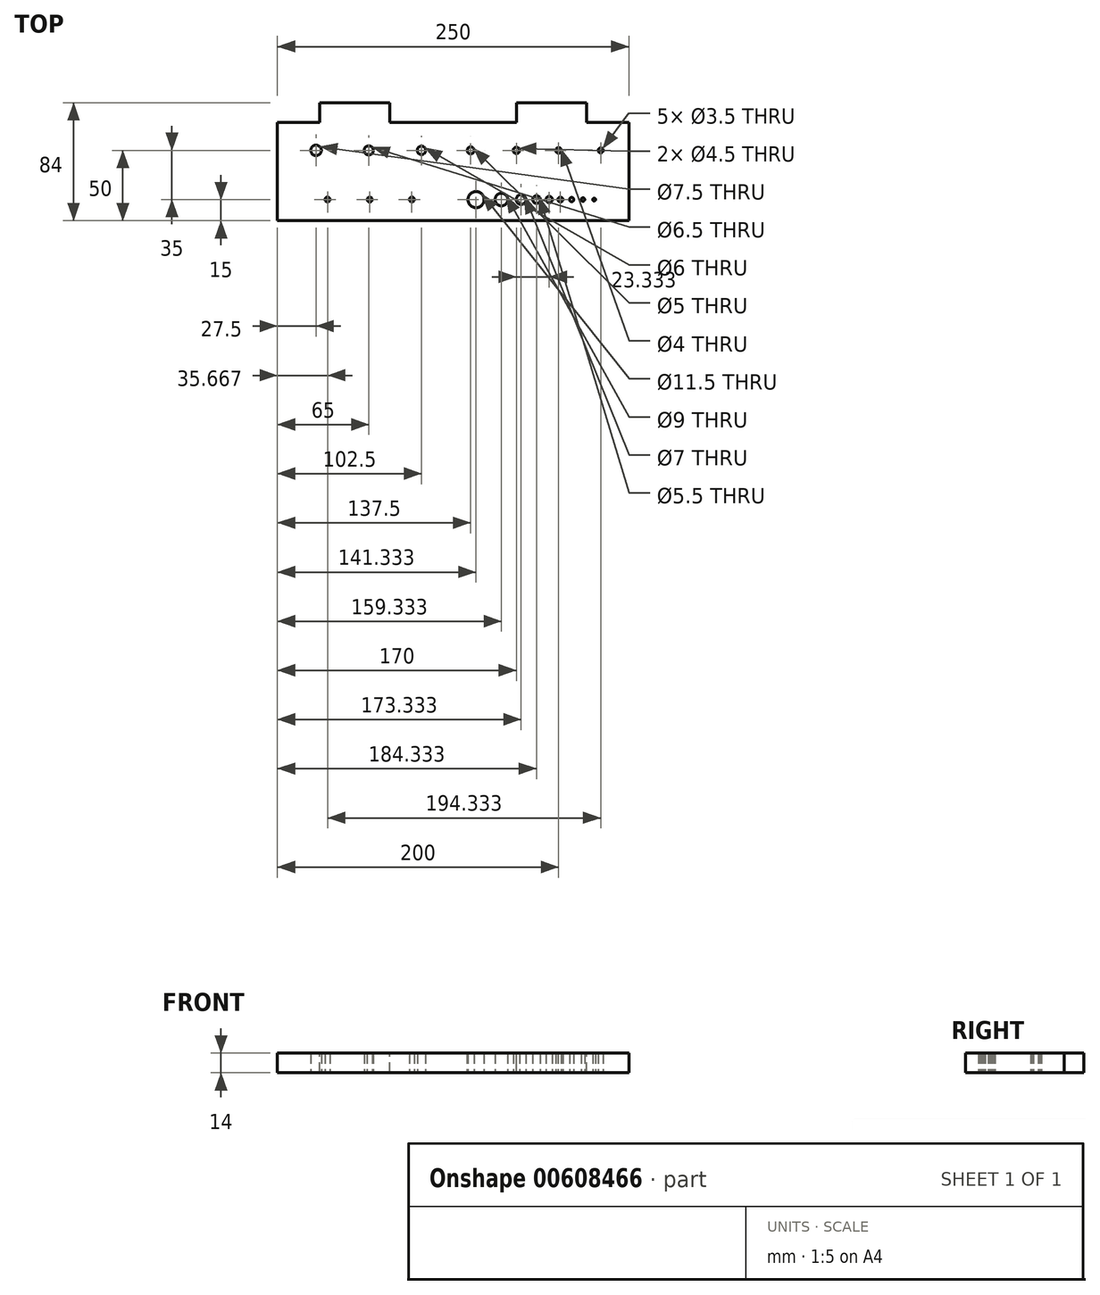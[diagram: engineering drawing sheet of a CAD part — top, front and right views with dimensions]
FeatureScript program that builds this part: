
annotation { "Feature Type Name" : "Feature", "Feature Type Description" : "" }
export const myFeature = defineFeature(function(context is Context, id is Id, definition is map)
    precondition{}
    {
        {
            var Q0;
            Q0=qCreatedBy(makeId("Top.planeOp"),FACE);
            var sketch = newSketch(context, id + "F0", { "sketchPlane" : qUnion([Q0])});
            skLineSegment(sketch, "E0.bottom", {"start": v(-125, 0) * mm, "end": v(125, 0) * mm});
            skLineSegment(sketch, "E0.top", {"start": v(-125, -70) * mm, "end": v(125, -70) * mm});
            skLineSegment(sketch, "E0.left", {"start": v(-125, 0) * mm, "end": v(-125, -70) * mm});
            skLineSegment(sketch, "E0.right", {"start": v(125, 0) * mm, "end": v(125, -70) * mm});
            skPoint(sketch, "E1", {"position": v(0, 0) * mm});
            skPoint(sketch, "E2", {"position": v(125, -35) * mm});
            skCircle(sketch, "E3", {"center": v(-97.5, -20) * mm, "radius": 3.75 * mm});
            skCircle(sketch, "E4", {"center": v(-60, -20) * mm, "radius": 3.25 * mm});
            skCircle(sketch, "E5", {"center": v(-22.5, -20) * mm, "radius": 3 * mm});
            skCircle(sketch, "E6", {"center": v(12.5, -20) * mm, "radius": 2.5 * mm});
            skCircle(sketch, "E7", {"center": v(45, -20) * mm, "radius": 2.25 * mm});
            skCircle(sketch, "E8", {"center": v(75, -20) * mm, "radius": 2 * mm});
            skCircle(sketch, "E9", {"center": v(105, -20) * mm, "radius": 1.75 * mm});
            skLineSegment(sketch, "E10", {"start": v(-115, -20) * mm, "end": v(-80, -20) * mm, "construction": true});
            skLineSegment(sketch, "E11", {"start": v(-80, -20) * mm, "end": v(-40, -20) * mm, "construction": true});
            skLineSegment(sketch, "E12", {"start": v(-40, -20) * mm, "end": v(-5, -20) * mm, "construction": true});
            skLineSegment(sketch, "E13", {"start": v(-5, -20) * mm, "end": v(30, -20) * mm, "construction": true});
            skLineSegment(sketch, "E14", {"start": v(30, -20) * mm, "end": v(60, -20) * mm, "construction": true});
            skLineSegment(sketch, "E15", {"start": v(60, -20) * mm, "end": v(90, -20) * mm, "construction": true});
            skLineSegment(sketch, "E16", {"start": v(90, -20) * mm, "end": v(120, -20) * mm, "construction": true});
            skPoint(sketch, "E17", {"position": v(-120, -20) * mm});
            skLineSegment(sketch, "E18", {"start": v(-120, -20) * mm, "end": v(-115, -20) * mm, "construction": true});
            skLineSegment(sketch, "E19", {"start": v(120, -20) * mm, "end": v(125, -20) * mm, "construction": true});
            skLineSegment(sketch, "E20", {"start": v(-120, -20) * mm, "end": v(-125, -20) * mm, "construction": true});
            skLineSegment(sketch, "E21", {"start": v(-125, -55) * mm, "end": v(-104.33, -55) * mm, "construction": true});
            skLineSegment(sketch, "E22", {"start": v(-104.33, -55) * mm, "end": v(-74.33, -55) * mm, "construction": true});
            skLineSegment(sketch, "E23", {"start": v(-74.33, -55) * mm, "end": v(-44.33, -55) * mm, "construction": true});
            skLineSegment(sketch, "E24", {"start": v(-44.33, -55) * mm, "end": v(-14.33, -55) * mm, "construction": true});
            skLineSegment(sketch, "E25", {"start": v(-14.33, -55) * mm, "end": v(6.33, -55) * mm, "construction": true});
            skLineSegment(sketch, "E26", {"start": v(6.33, -55) * mm, "end": v(26.33, -55) * mm, "construction": true});
            skLineSegment(sketch, "E27", {"start": v(26.33, -55) * mm, "end": v(42.33, -55) * mm, "construction": true});
            skLineSegment(sketch, "E28", {"start": v(42.33, -55) * mm, "end": v(54.33, -55) * mm, "construction": true});
            skLineSegment(sketch, "E29", {"start": v(54.33, -55) * mm, "end": v(64.33, -55) * mm, "construction": true});
            skLineSegment(sketch, "E30", {"start": v(64.33, -55) * mm, "end": v(72.33, -55) * mm, "construction": true});
            skLineSegment(sketch, "E31", {"start": v(72.33, -55) * mm, "end": v(80.33, -55) * mm, "construction": true});
            skLineSegment(sketch, "E32", {"start": v(80.33, -55) * mm, "end": v(88.33, -55) * mm, "construction": true});
            skLineSegment(sketch, "E33", {"start": v(88.33, -55) * mm, "end": v(96.33, -55) * mm, "construction": true});
            skLineSegment(sketch, "E34", {"start": v(96.33, -55) * mm, "end": v(104.33, -55) * mm, "construction": true});
            skLineSegment(sketch, "E35", {"start": v(104.33, -55) * mm, "end": v(125, -55) * mm, "construction": true});
            skCircle(sketch, "E36", {"center": v(-89.33, -55) * mm, "radius": 1.75 * mm});
            skCircle(sketch, "E37", {"center": v(-59.33, -55) * mm, "radius": 1.75 * mm});
            skCircle(sketch, "E38", {"center": v(-29.33, -55) * mm, "radius": 1.75 * mm});
            skCircle(sketch, "E39", {"center": v(16.33, -55) * mm, "radius": 5.75 * mm});
            skCircle(sketch, "E40", {"center": v(34.33, -55) * mm, "radius": 4.5 * mm});
            skCircle(sketch, "E41", {"center": v(48.33, -55) * mm, "radius": 3.5 * mm});
            skCircle(sketch, "E42", {"center": v(59.33, -55) * mm, "radius": 2.75 * mm});
            skCircle(sketch, "E43", {"center": v(68.33, -55) * mm, "radius": 2.25 * mm});
            skCircle(sketch, "E44", {"center": v(76.33, -55) * mm, "radius": 1.75 * mm});
            skCircle(sketch, "E45", {"center": v(84.33, -55) * mm, "radius": 1.5 * mm});
            skCircle(sketch, "E46", {"center": v(92.33, -55) * mm, "radius": 1.25 * mm});
            skCircle(sketch, "E47", {"center": v(100.33, -55) * mm, "radius": 1 * mm});
            skSolve(sketch);
        }
        {
            var Q0;
            Q0=makeQuery(id+"F0.imprint","IMPRINT",FACE,{"disambiguationData":[TD([[makeQuery(id+"F0.imprint","IMPRINT",EDGE,{"derivedFrom":sQuery(id+"F0.wireOp",EDGE,"E0.bottom")}),-1.0]])]});
            extrude(context, id + "F1", {"entities" : qUnion([Q0]), "depth" : 14 * mm, "offsetDistance" : 25 * mm});
        }
        {
            var Q0;
            Q0=makeQuery(id+"F1.opExtrude","SWEPT_FACE",FACE,{"disambiguationData":[OSD([sQuery(id+"F0.wireOp",EDGE,"E0.bottom")])]});
            var sketch = newSketch(context, id + "F2", { "sketchPlane" : qUnion([Q0])});
            skLineSegment(sketch, "E48.bottom", {"start": v(95, 0) * mm, "end": v(45, 0) * mm});
            skLineSegment(sketch, "E48.top", {"start": v(95, 14) * mm, "end": v(45, 14) * mm});
            skLineSegment(sketch, "E48.left", {"start": v(95, 0) * mm, "end": v(95, 14) * mm});
            skLineSegment(sketch, "E48.right", {"start": v(45, 0) * mm, "end": v(45, 14) * mm});
            skLineSegment(sketch, "E49.MirrorCS", {"start": v(-95, 0) * mm, "end": v(-45, 0) * mm});
            skLineSegment(sketch, "E50.MirrorCS", {"start": v(-95, 14) * mm, "end": v(-45, 14) * mm});
            skLineSegment(sketch, "E51.MirrorCS", {"start": v(-45, 0) * mm, "end": v(-45, 14) * mm});
            skLineSegment(sketch, "E52.MirrorCS", {"start": v(-95, 0) * mm, "end": v(-95, 14) * mm});
            skSolve(sketch);
        }
        {
            var Q0;
            Q0=makeQuery(id+"F2.imprint","IMPRINT",FACE,{"disambiguationData":[TD([[makeQuery(id+"F2.imprint","IMPRINT",EDGE,{"derivedFrom":sQuery(id+"F2.wireOp",EDGE,"E48.bottom")}),-1.0]])]});
            var Q1;
            Q1=makeQuery(id+"F2.imprint","IMPRINT",FACE,{"disambiguationData":[TD([[makeQuery(id+"F2.imprint","IMPRINT",EDGE,{"derivedFrom":sQuery(id+"F2.wireOp",EDGE,"E49.MirrorCS")}),-1.0]])]});
            extrude(context, id + "F3", {"entities" : qUnion([Q0, Q1]), "operationType" : NewBodyOperationType.ADD, "depth" : 14 * mm, "offsetDistance" : 25 * mm});
        }
    });
